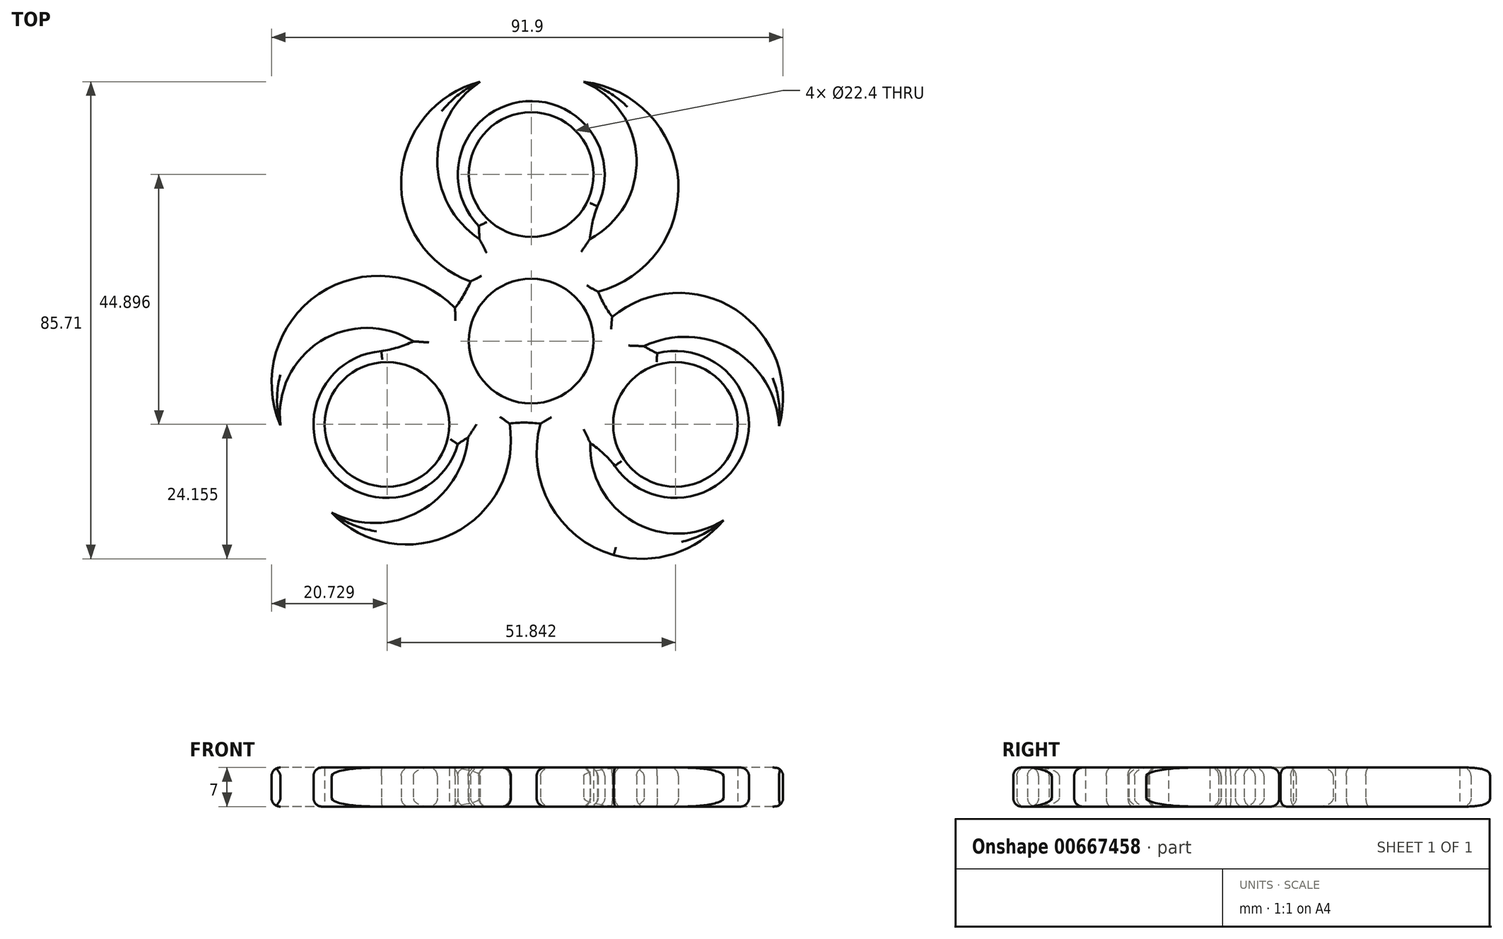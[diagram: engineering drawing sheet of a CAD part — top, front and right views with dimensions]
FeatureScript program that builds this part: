
annotation { "Feature Type Name" : "Feature", "Feature Type Description" : "" }
export const myFeature = defineFeature(function(context is Context, id is Id, definition is map)
    precondition{}
    {
        {
            var Q0;
            Q0=qCreatedBy(makeId("Top.planeOp"),FACE);
            var sketch = newSketch(context, id + "F0", { "sketchPlane" : qUnion([Q0])});
            skCircle(sketch, "E0", {"center": v(0, 0) * mm, "radius": 11.2 * mm});
            skCircle(sketch, "E1", {"center": v(0, 29.93) * mm, "radius": 11.2 * mm});
            skArc(sketch, "E2", {"start": v(11.9, 24.23) * mm, "mid": v(-2.15, 42.95) * mm, "end": v(-9.43, 20.7) * mm});
            skArc(sketch, "E3.1.0", {"start": v(-26.93, -1.8) * mm, "mid": v(-36.12, -23.34) * mm, "end": v(-13.2, -18.52) * mm});
            skCircle(sketch, "E3.1.1", {"center": v(-25.92, -14.97) * mm, "radius": 11.2 * mm});
            skArc(sketch, "E3.2.0", {"start": v(15.03, -22.42) * mm, "mid": v(38.28, -19.61) * mm, "end": v(22.64, -2.18) * mm});
            skCircle(sketch, "E3.2.1", {"center": v(25.92, -14.97) * mm, "radius": 11.2 * mm});
            skArc(sketch, "E4", {"start": v(11.9, 24.23) * mm, "mid": v(11.01, 21.34) * mm, "end": v(10.55, 18.36) * mm});
            skArc(sketch, "E5.1.0", {"start": v(-26.93, -1.8) * mm, "mid": v(-17.27, 2.36) * mm, "end": v(-10.9, 10.74) * mm});
            skArc(sketch, "E5.2.0", {"start": v(15.03, -22.42) * mm, "mid": v(6.57, -16.13) * mm, "end": v(-3.88, -14.82) * mm});
            skArc(sketch, "E6", {"start": v(-9.17, 46.59) * mm, "mid": v(-23.36, 29.31) * mm, "end": v(-10.9, 10.74) * mm});
            skArc(sketch, "E7", {"start": v(-9.17, 46.59) * mm, "mid": v(-16.87, 32.52) * mm, "end": v(-9.34, 18.36) * mm});
            skArc(sketch, "E8", {"start": v(10.55, 18.36) * mm, "mid": v(18.91, 32.82) * mm, "end": v(9.44, 46.59) * mm});
            skPoint(sketch, "E8.startSnap0", {"position": v(13.3, 18.36) * mm});
            skArc(sketch, "E9", {"start": v(12, 8.88) * mm, "mid": v(26.4, 28.8) * mm, "end": v(9.44, 46.59) * mm});
            skArc(sketch, "E10.1.2", {"start": v(-35.86, -30.83) * mm, "mid": v(-19.83, -30.46) * mm, "end": v(-11.34, -16.86) * mm});
            skArc(sketch, "E10.1.3", {"start": v(-35.86, -30.83) * mm, "mid": v(-13.8, -34.47) * mm, "end": v(-3.95, -14.41) * mm});
            skArc(sketch, "E10.2.0", {"start": v(1.29, -14.72) * mm, "mid": v(11.33, -37.16) * mm, "end": v(35.22, -31.35) * mm});
            skArc(sketch, "E10.2.1", {"start": v(10.22, -18.2) * mm, "mid": v(18.57, -32.68) * mm, "end": v(35.22, -31.35) * mm});
            skArc(sketch, "E10.2.2", {"start": v(44.53, -15.24) * mm, "mid": v(36.2, -1.54) * mm, "end": v(20.16, -0.98) * mm});
            skArc(sketch, "E10.2.3", {"start": v(44.53, -15.24) * mm, "mid": v(36.66, 5.69) * mm, "end": v(14.35, 4.19) * mm});
            skPoint(sketch, "E10.center", {"position": v(-0.17, 0.17) * mm});
            skPoint(sketch, "E11.orphan", {"position": v(35.94, 18.36) * mm});
            skLineSegment(sketch, "E12.trimOffspring", {"start": v(10.55, 18.36) * mm, "end": v(13.3, 18.36) * mm, "construction": true});
            skArc(sketch, "E13.trimOffspring", {"start": v(-9.34, 18.36) * mm, "mid": v(-9.35, 19.53) * mm, "end": v(-9.43, 20.7) * mm});
            skArc(sketch, "E14.trimOffspring", {"start": v(12, 8.88) * mm, "mid": v(13.13, 6.54) * mm, "end": v(14.55, 4.35) * mm});
            skArc(sketch, "E15.trimOffspring", {"start": v(20.28, -0.92) * mm, "mid": v(21.44, -1.59) * mm, "end": v(22.64, -2.18) * mm});
            skArc(sketch, "E16.trimOffspring", {"start": v(-11.37, -17.34) * mm, "mid": v(-12.3, -17.9) * mm, "end": v(-13.2, -18.52) * mm});
            skArc(sketch, "E17.1.0", {"start": v(-13.7, 5.95) * mm, "mid": v(-38.15, 8.47) * mm, "end": v(-45.06, -15.12) * mm});
            skArc(sketch, "E17.1.1", {"start": v(-21.17, -0.05) * mm, "mid": v(-37.88, -0.03) * mm, "end": v(-45.06, -15.12) * mm});
            skArc(sketch, "E17.2.0", {"start": v(1.7, -14.84) * mm, "mid": v(11.74, -37.27) * mm, "end": v(35.63, -31.47) * mm});
            skArc(sketch, "E17.2.1", {"start": v(10.63, -18.31) * mm, "mid": v(18.97, -32.79) * mm, "end": v(35.63, -31.47) * mm});
            skSolve(sketch);
        }
        {
            var Q0;
            Q0=makeQuery(id+"F0.imprint","IMPRINT",FACE,{"disambiguationData":[TD([[makeQuery(id+"F0.imprint","IMPRINT",EDGE,{"derivedFrom":sQuery(id+"F0.wireOp",EDGE,"E0")}),-1.0]])]});
            var Q1;
            {var subQ0=sQuery(id+"F0.wireOp",EDGE,"E17.1.0");Q1=makeQuery(id+"F0.imprint","IMPRINT",FACE,{"disambiguationData":[TD([[makeQuery(id+"F0.imprint","IMPRINT",EDGE,{"derivedFrom":subQ0}),1.0]])]});}
            var Q2;
            {var subQ1=sQuery(id+"F0.wireOp",EDGE,"E5.2.0");var subQ4=sQuery(id+"F0.wireOp",EDGE,"E17.2.0");var subQ5=makeQuery(id+"F0.imprint","INTERSECT",VERTEX,{"derivedFrom":[subQ1,subQ4]});Q2=makeQuery(id+"F0.imprint","IMPRINT",FACE,{"disambiguationData":[TD([[makeQuery(id+"F0.imprint","IMPRINT",EDGE,{"disambiguationData":[TD([[subQ5,1.0]])],"derivedFrom":subQ1}),1.0]])]});}
            extrude(context, id + "F1", {"entities" : qUnion([Q0, Q1, Q2]), "depth" : 7 * mm, "offsetDistance" : 25 * mm});
        }
        {
            var Q0;
            Q0=makeQuery(id+"F1.opExtrude","CAP_EDGE",EDGE,{"disambiguationData":[OSD([sQuery(id+"F0.wireOp",EDGE,"E6")])],"isStart":false});
            var Q1;
            Q1=makeQuery(id+"F1.opExtrude","CAP_EDGE",EDGE,{"disambiguationData":[OSD([sQuery(id+"F0.wireOp",EDGE,"E7")])],"isStart":false});
            var Q2;
            Q2=makeQuery(id+"F1.opExtrude","CAP_EDGE",EDGE,{"disambiguationData":[OSD([sQuery(id+"F0.wireOp",EDGE,"E2")])],"isStart":false});
            var Q3;
            Q3=makeQuery(id+"F1.opExtrude","CAP_EDGE",EDGE,{"disambiguationData":[OSD([sQuery(id+"F0.wireOp",EDGE,"E4")])],"isStart":false});
            var Q4;
            Q4=makeQuery(id+"F1.opExtrude","CAP_EDGE",EDGE,{"disambiguationData":[OSD([sQuery(id+"F0.wireOp",EDGE,"E13.trimOffspring")])],"isStart":false});
            var Q5;
            Q5=makeQuery(id+"F1.opExtrude","CAP_EDGE",EDGE,{"disambiguationData":[OSD([sQuery(id+"F0.wireOp",EDGE,"E8")])],"isStart":false});
            var Q6;
            Q6=makeQuery(id+"F1.opExtrude","CAP_EDGE",EDGE,{"disambiguationData":[OSD([sQuery(id+"F0.wireOp",EDGE,"E9")])],"isStart":false});
            var Q7;
            {var subQ0=sQuery(id+"F0.wireOp",EDGE,"E5.1.0");Q7=makeQuery(id+"F1.opExtrude","CAP_EDGE",EDGE,{"disambiguationData":[OSD([subQ0]),TDD([makeQuery(id+"F0.imprint","IMPRINT",EDGE,{"disambiguationData":[TD([[makeQuery(id+"F0.imprint","INTERSECT",VERTEX,{"derivedFrom":[subQ0,sQuery(id+"F0.wireOp",EDGE,"E6")]}),1.0]])],"derivedFrom":subQ0})])],"isStart":false});}
            var Q8;
            Q8=makeQuery(id+"F1.opExtrude","CAP_EDGE",EDGE,{"disambiguationData":[OSD([sQuery(id+"F0.wireOp",EDGE,"E17.1.0")])],"isStart":false});
            var Q9;
            Q9=makeQuery(id+"F1.opExtrude","CAP_EDGE",EDGE,{"disambiguationData":[OSD([sQuery(id+"F0.wireOp",EDGE,"E17.1.1")])],"isStart":false});
            var Q10;
            {var subQ0=sQuery(id+"F0.wireOp",EDGE,"E5.1.0");Q10=makeQuery(id+"F1.opExtrude","CAP_EDGE",EDGE,{"disambiguationData":[OSD([subQ0]),TDD([makeQuery(id+"F0.imprint","IMPRINT",EDGE,{"disambiguationData":[TD([[makeQuery(id+"F0.imprint","INTERSECT",VERTEX,{"derivedFrom":[sQuery(id+"F0.wireOp",EDGE,"E3.1.0"),subQ0]}),-1.0]])],"derivedFrom":subQ0})])],"isStart":false});}
            var Q11;
            Q11=makeQuery(id+"F1.opExtrude","CAP_EDGE",EDGE,{"disambiguationData":[OSD([sQuery(id+"F0.wireOp",EDGE,"E3.1.0")])],"isStart":false});
            var Q12;
            Q12=makeQuery(id+"F1.opExtrude","CAP_EDGE",EDGE,{"disambiguationData":[OSD([sQuery(id+"F0.wireOp",EDGE,"E16.trimOffspring")])],"isStart":false});
            var Q13;
            Q13=makeQuery(id+"F1.opExtrude","CAP_EDGE",EDGE,{"disambiguationData":[OSD([sQuery(id+"F0.wireOp",EDGE,"E10.1.2")])],"isStart":false});
            var Q14;
            Q14=makeQuery(id+"F1.opExtrude","CAP_EDGE",EDGE,{"disambiguationData":[OSD([sQuery(id+"F0.wireOp",EDGE,"E10.1.3")])],"isStart":false});
            var Q15;
            Q15=makeQuery(id+"F1.opExtrude","CAP_EDGE",EDGE,{"disambiguationData":[OSD([sQuery(id+"F0.wireOp",EDGE,"E17.2.0")])],"isStart":false});
            var Q16;
            {var subQ0=sQuery(id+"F0.wireOp",EDGE,"E5.2.0");Q16=makeQuery(id+"F1.opExtrude","CAP_EDGE",EDGE,{"disambiguationData":[OSD([subQ0]),TDD([makeQuery(id+"F0.imprint","IMPRINT",EDGE,{"disambiguationData":[TD([[makeQuery(id+"F0.imprint","INTERSECT",VERTEX,{"derivedFrom":[subQ0,sQuery(id+"F0.wireOp",EDGE,"E17.2.0")]}),-1.0]])],"derivedFrom":subQ0}),makeQuery(id+"F0.imprint","IMPRINT",EDGE,{"disambiguationData":[TD([[makeQuery(id+"F0.imprint","INTERSECT",VERTEX,{"derivedFrom":[subQ0,sQuery(id+"F0.wireOp",EDGE,"E10.1.3")]}),1.0]])],"derivedFrom":subQ0})])],"isStart":false});}
            var Q17;
            Q17=makeQuery(id+"F1.opExtrude","CAP_EDGE",EDGE,{"disambiguationData":[OSD([sQuery(id+"F0.wireOp",EDGE,"E10.2.0")])],"isStart":false});
            var Q18;
            Q18=makeQuery(id+"F1.opExtrude","CAP_EDGE",EDGE,{"disambiguationData":[OSD([sQuery(id+"F0.wireOp",EDGE,"E17.2.1")])],"isStart":false});
            var Q19;
            Q19=makeQuery(id+"F1.opExtrude","CAP_EDGE",EDGE,{"disambiguationData":[OSD([sQuery(id+"F0.wireOp",EDGE,"E3.2.0")])],"isStart":false});
            var Q20;
            {var subQ0=sQuery(id+"F0.wireOp",EDGE,"E5.2.0");Q20=makeQuery(id+"F1.opExtrude","CAP_EDGE",EDGE,{"disambiguationData":[OSD([subQ0]),TDD([makeQuery(id+"F0.imprint","IMPRINT",EDGE,{"disambiguationData":[TD([[makeQuery(id+"F0.imprint","INTERSECT",VERTEX,{"derivedFrom":[sQuery(id+"F0.wireOp",EDGE,"E3.2.0"),subQ0]}),-1.0]])],"derivedFrom":subQ0})])],"isStart":false});}
            var Q21;
            Q21=makeQuery(id+"F1.opExtrude","CAP_EDGE",EDGE,{"disambiguationData":[OSD([sQuery(id+"F0.wireOp",EDGE,"E15.trimOffspring")])],"isStart":false});
            var Q22;
            Q22=makeQuery(id+"F1.opExtrude","CAP_EDGE",EDGE,{"disambiguationData":[OSD([sQuery(id+"F0.wireOp",EDGE,"E10.2.2")])],"isStart":false});
            var Q23;
            Q23=makeQuery(id+"F1.opExtrude","CAP_EDGE",EDGE,{"disambiguationData":[OSD([sQuery(id+"F0.wireOp",EDGE,"E10.2.3")])],"isStart":false});
            var Q24;
            Q24=makeQuery(id+"F1.opExtrude","CAP_EDGE",EDGE,{"disambiguationData":[OSD([sQuery(id+"F0.wireOp",EDGE,"E14.trimOffspring")])],"isStart":false});
            fillet(context, id + "F2", {"entities" : qUnion([Q0, Q1, Q2, Q3, Q4, Q5, Q6, Q7, Q8, Q9, Q10, Q11, Q12, Q13, Q14, Q15, Q16, Q17, Q18, Q19, Q20, Q21, Q22, Q23, Q24]), "radius" : 1.5 * mm, "tangentPropagation" : true, "allowEdgeOverflow" : false});
        }
        {
            var Q0;
            Q0=makeQuery(id+"F1.opExtrude","CAP_EDGE",EDGE,{"disambiguationData":[OSD([sQuery(id+"F0.wireOp",EDGE,"E9")])],"isStart":true});
            var Q1;
            Q1=makeQuery(id+"F1.opExtrude","CAP_EDGE",EDGE,{"disambiguationData":[OSD([sQuery(id+"F0.wireOp",EDGE,"E8")])],"isStart":true});
            var Q2;
            Q2=makeQuery(id+"F1.opExtrude","CAP_EDGE",EDGE,{"disambiguationData":[OSD([sQuery(id+"F0.wireOp",EDGE,"E4")])],"isStart":true});
            var Q3;
            Q3=makeQuery(id+"F1.opExtrude","CAP_EDGE",EDGE,{"disambiguationData":[OSD([sQuery(id+"F0.wireOp",EDGE,"E2")])],"isStart":true});
            var Q4;
            Q4=makeQuery(id+"F1.opExtrude","CAP_EDGE",EDGE,{"disambiguationData":[OSD([sQuery(id+"F0.wireOp",EDGE,"E13.trimOffspring")])],"isStart":true});
            var Q5;
            Q5=makeQuery(id+"F1.opExtrude","CAP_EDGE",EDGE,{"disambiguationData":[OSD([sQuery(id+"F0.wireOp",EDGE,"E7")])],"isStart":true});
            var Q6;
            Q6=makeQuery(id+"F1.opExtrude","CAP_EDGE",EDGE,{"disambiguationData":[OSD([sQuery(id+"F0.wireOp",EDGE,"E6")])],"isStart":true});
            var Q7;
            {var subQ0=sQuery(id+"F0.wireOp",EDGE,"E5.1.0");Q7=makeQuery(id+"F1.opExtrude","CAP_EDGE",EDGE,{"disambiguationData":[OSD([subQ0]),TDD([makeQuery(id+"F0.imprint","IMPRINT",EDGE,{"disambiguationData":[TD([[makeQuery(id+"F0.imprint","INTERSECT",VERTEX,{"derivedFrom":[subQ0,sQuery(id+"F0.wireOp",EDGE,"E6")]}),1.0]])],"derivedFrom":subQ0})])],"isStart":true});}
            var Q8;
            Q8=makeQuery(id+"F1.opExtrude","CAP_EDGE",EDGE,{"disambiguationData":[OSD([sQuery(id+"F0.wireOp",EDGE,"E17.1.0")])],"isStart":true});
            var Q9;
            Q9=makeQuery(id+"F1.opExtrude","CAP_EDGE",EDGE,{"disambiguationData":[OSD([sQuery(id+"F0.wireOp",EDGE,"E17.1.1")])],"isStart":true});
            var Q10;
            {var subQ0=sQuery(id+"F0.wireOp",EDGE,"E5.1.0");Q10=makeQuery(id+"F1.opExtrude","CAP_EDGE",EDGE,{"disambiguationData":[OSD([subQ0]),TDD([makeQuery(id+"F0.imprint","IMPRINT",EDGE,{"disambiguationData":[TD([[makeQuery(id+"F0.imprint","INTERSECT",VERTEX,{"derivedFrom":[sQuery(id+"F0.wireOp",EDGE,"E3.1.0"),subQ0]}),-1.0]])],"derivedFrom":subQ0})])],"isStart":true});}
            var Q11;
            Q11=makeQuery(id+"F1.opExtrude","CAP_EDGE",EDGE,{"disambiguationData":[OSD([sQuery(id+"F0.wireOp",EDGE,"E3.1.0")])],"isStart":true});
            var Q12;
            Q12=makeQuery(id+"F1.opExtrude","CAP_EDGE",EDGE,{"disambiguationData":[OSD([sQuery(id+"F0.wireOp",EDGE,"E16.trimOffspring")])],"isStart":true});
            var Q13;
            Q13=makeQuery(id+"F1.opExtrude","CAP_EDGE",EDGE,{"disambiguationData":[OSD([sQuery(id+"F0.wireOp",EDGE,"E10.1.2")])],"isStart":true});
            var Q14;
            Q14=makeQuery(id+"F1.opExtrude","CAP_EDGE",EDGE,{"disambiguationData":[OSD([sQuery(id+"F0.wireOp",EDGE,"E10.1.3")])],"isStart":true});
            var Q15;
            {var subQ0=sQuery(id+"F0.wireOp",EDGE,"E5.2.0");Q15=makeQuery(id+"F1.opExtrude","CAP_EDGE",EDGE,{"disambiguationData":[OSD([subQ0]),TDD([makeQuery(id+"F0.imprint","IMPRINT",EDGE,{"disambiguationData":[TD([[makeQuery(id+"F0.imprint","INTERSECT",VERTEX,{"derivedFrom":[subQ0,sQuery(id+"F0.wireOp",EDGE,"E17.2.0")]}),-1.0]])],"derivedFrom":subQ0}),makeQuery(id+"F0.imprint","IMPRINT",EDGE,{"disambiguationData":[TD([[makeQuery(id+"F0.imprint","INTERSECT",VERTEX,{"derivedFrom":[subQ0,sQuery(id+"F0.wireOp",EDGE,"E10.1.3")]}),1.0]])],"derivedFrom":subQ0})])],"isStart":true});}
            var Q16;
            Q16=makeQuery(id+"F1.opExtrude","CAP_EDGE",EDGE,{"disambiguationData":[OSD([sQuery(id+"F0.wireOp",EDGE,"E17.2.0")])],"isStart":true});
            var Q17;
            Q17=makeQuery(id+"F1.opExtrude","CAP_EDGE",EDGE,{"disambiguationData":[OSD([sQuery(id+"F0.wireOp",EDGE,"E10.2.0")])],"isStart":true});
            var Q18;
            {var subQ0=sQuery(id+"F0.wireOp",EDGE,"E5.2.0");Q18=makeQuery(id+"F1.opExtrude","CAP_EDGE",EDGE,{"disambiguationData":[OSD([subQ0]),TDD([makeQuery(id+"F0.imprint","IMPRINT",EDGE,{"disambiguationData":[TD([[makeQuery(id+"F0.imprint","INTERSECT",VERTEX,{"derivedFrom":[sQuery(id+"F0.wireOp",EDGE,"E3.2.0"),subQ0]}),-1.0]])],"derivedFrom":subQ0})])],"isStart":true});}
            var Q19;
            Q19=makeQuery(id+"F1.opExtrude","CAP_EDGE",EDGE,{"disambiguationData":[OSD([sQuery(id+"F0.wireOp",EDGE,"E17.2.1")])],"isStart":true});
            var Q20;
            Q20=makeQuery(id+"F1.opExtrude","CAP_EDGE",EDGE,{"disambiguationData":[OSD([sQuery(id+"F0.wireOp",EDGE,"E3.2.0")])],"isStart":true});
            var Q21;
            Q21=makeQuery(id+"F1.opExtrude","CAP_EDGE",EDGE,{"disambiguationData":[OSD([sQuery(id+"F0.wireOp",EDGE,"E15.trimOffspring")])],"isStart":true});
            var Q22;
            Q22=makeQuery(id+"F1.opExtrude","CAP_EDGE",EDGE,{"disambiguationData":[OSD([sQuery(id+"F0.wireOp",EDGE,"E10.2.2")])],"isStart":true});
            var Q23;
            Q23=makeQuery(id+"F1.opExtrude","CAP_EDGE",EDGE,{"disambiguationData":[OSD([sQuery(id+"F0.wireOp",EDGE,"E10.2.3")])],"isStart":true});
            var Q24;
            Q24=makeQuery(id+"F1.opExtrude","CAP_EDGE",EDGE,{"disambiguationData":[OSD([sQuery(id+"F0.wireOp",EDGE,"E14.trimOffspring")])],"isStart":true});
            fillet(context, id + "F3", {"entities" : qUnion([Q0, Q1, Q2, Q3, Q4, Q5, Q6, Q7, Q8, Q9, Q10, Q11, Q12, Q13, Q14, Q15, Q16, Q17, Q18, Q19, Q20, Q21, Q22, Q23, Q24]), "radius" : 1.5 * mm, "tangentPropagation" : true, "allowEdgeOverflow" : false});
        }
    });
